# Revit family: Electronics_Commercial-Audio_Biamp_Digital-Priority-Emergency-Extender_Dipex
name_source: partatom
category: Communication Devices
units: mm (PartAtom-declared; Revit-internal decimal feet)

## family parameters
Cut with Voids When Loaded = No
Host = Face
Maintain Annotation Orientation = No
OmniClass Number = 23.85.10.11.14
OmniClass Title = Audio Equipment
Part Type = Normal
Room Calculation Point = No
Round Connector Dimension = Use Diameter
Shared = No

## types (1)
- DIPEX
    Apparent Load = 0 VA
    Buttons = 1 test button
    Cable type = CAT5
    Connector Description = 24 VDC jack; Power
    Current = 0.00075 A
    Default Elevation = 4' - 0"
    Depth = 0' - 4"
    Description = DIPEX Digital Priority/Emergency Extender for AUDIOCONTROL12.8
    Frequency range = 20 Hz - 20 kHz
    Height = 0' - 1 1/2"
    Housing Material = Biamp - Metal - Black
    Indicator = Power - status
    Input impedance in Ohm = 100k
    Inputs = Bal. line
    Manufacturer = Biamp
    Max Power Consumption = 0 W
    Model = DIPEX
    Number of Poles = 1
    Power Factor = 1
    Power type = Phantom or external power supply
    Product Documentation Link = https://downloads.biamp.com
    Product Page URL = https://www.biamp.com
    Product data url = https://www.bimobject.com
    Sensitivity = 100mV - 1V RMS (0 dBV)
    Supported main unit = AUDIOCONTROL12.8
    URL = https://www.biamp.com
    Voltage = 24 V
    Weight = 0.77 lb
    Width = 0' - 5"
    Zones = Up to 24

## geometry (parser evidence)
native form markers: Blend x2, Sweep x3
no freeform markers — native parametric forms only
